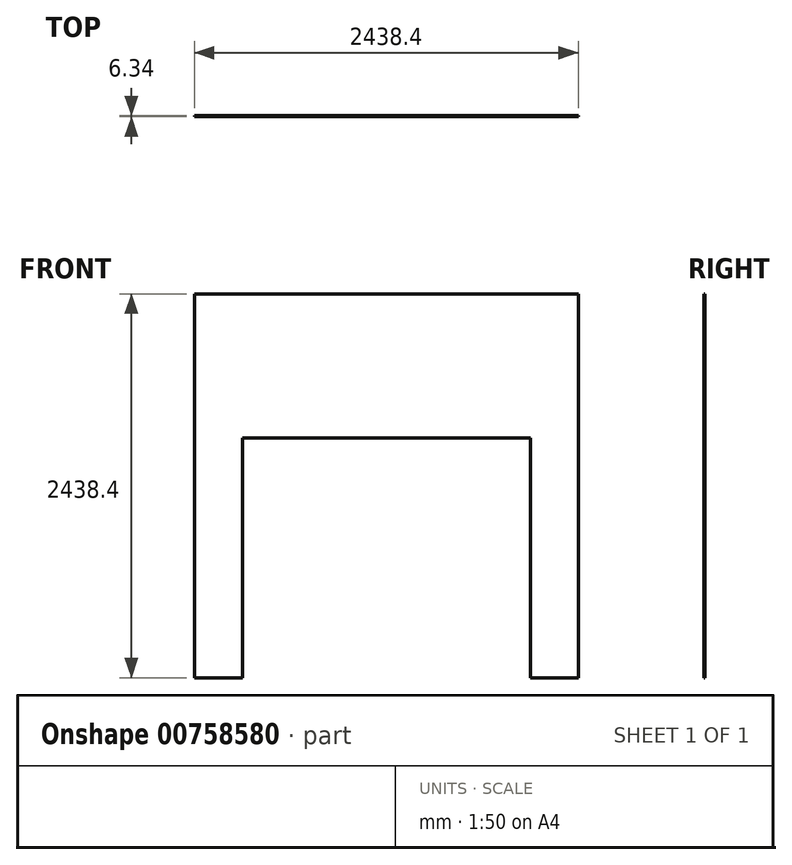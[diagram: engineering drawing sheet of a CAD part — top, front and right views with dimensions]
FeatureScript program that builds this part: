
annotation { "Feature Type Name" : "Feature", "Feature Type Description" : "" }
export const myFeature = defineFeature(function(context is Context, id is Id, definition is map)
    precondition{}
    {
        {
            var Q0;
            Q0=qCreatedBy(makeId("Front.planeOp"),FACE);
            var sketch = newSketch(context, id + "F0", { "sketchPlane" : qUnion([Q0])});
            skLineSegment(sketch, "E0.bottom", {"start": v(-1219.2, 1219.2) * mm, "end": v(1219.2, 1219.2) * mm});
            skLineSegment(sketch, "E0.top", {"start": v(-1219.2, -1219.2) * mm, "end": v(1219.2, -1219.2) * mm});
            skLineSegment(sketch, "E0.left", {"start": v(-1219.2, 1219.2) * mm, "end": v(-1219.2, -1219.2) * mm});
            skLineSegment(sketch, "E0.right", {"start": v(1219.2, 1219.2) * mm, "end": v(1219.2, -1219.2) * mm});
            skPoint(sketch, "E0.middle", {"position": v(0, 0) * mm});
            skLineSegment(sketch, "E1.bottom", {"start": v(-914.4, -1219.2) * mm, "end": v(914.4, -1219.2) * mm});
            skLineSegment(sketch, "E2", {"start": v(-914.4, -1219.2) * mm, "end": v(-914.4, 304.8) * mm});
            skLineSegment(sketch, "E3", {"start": v(914.4, -1219.2) * mm, "end": v(914.4, 304.8) * mm});
            skLineSegment(sketch, "E4", {"start": v(-914.4, 304.8) * mm, "end": v(914.4, 304.8) * mm});
            skSolve(sketch);
        }
        {
            var Q0;
            Q0=makeQuery(id+"F0.imprint","IMPRINT",FACE,{"disambiguationData":[TD([[makeQuery(id+"F0.imprint","IMPRINT",EDGE,{"derivedFrom":sQuery(id+"F0.wireOp",EDGE,"E0.bottom")}),-1.0]])]});
            extrude(context, id + "F1", {"entities" : qUnion([Q0]), "endBound" : BoundingType.SYMMETRIC, "depth" : 6.35 * mm, "offsetDistance" : 25.4 * mm});
        }
    });
